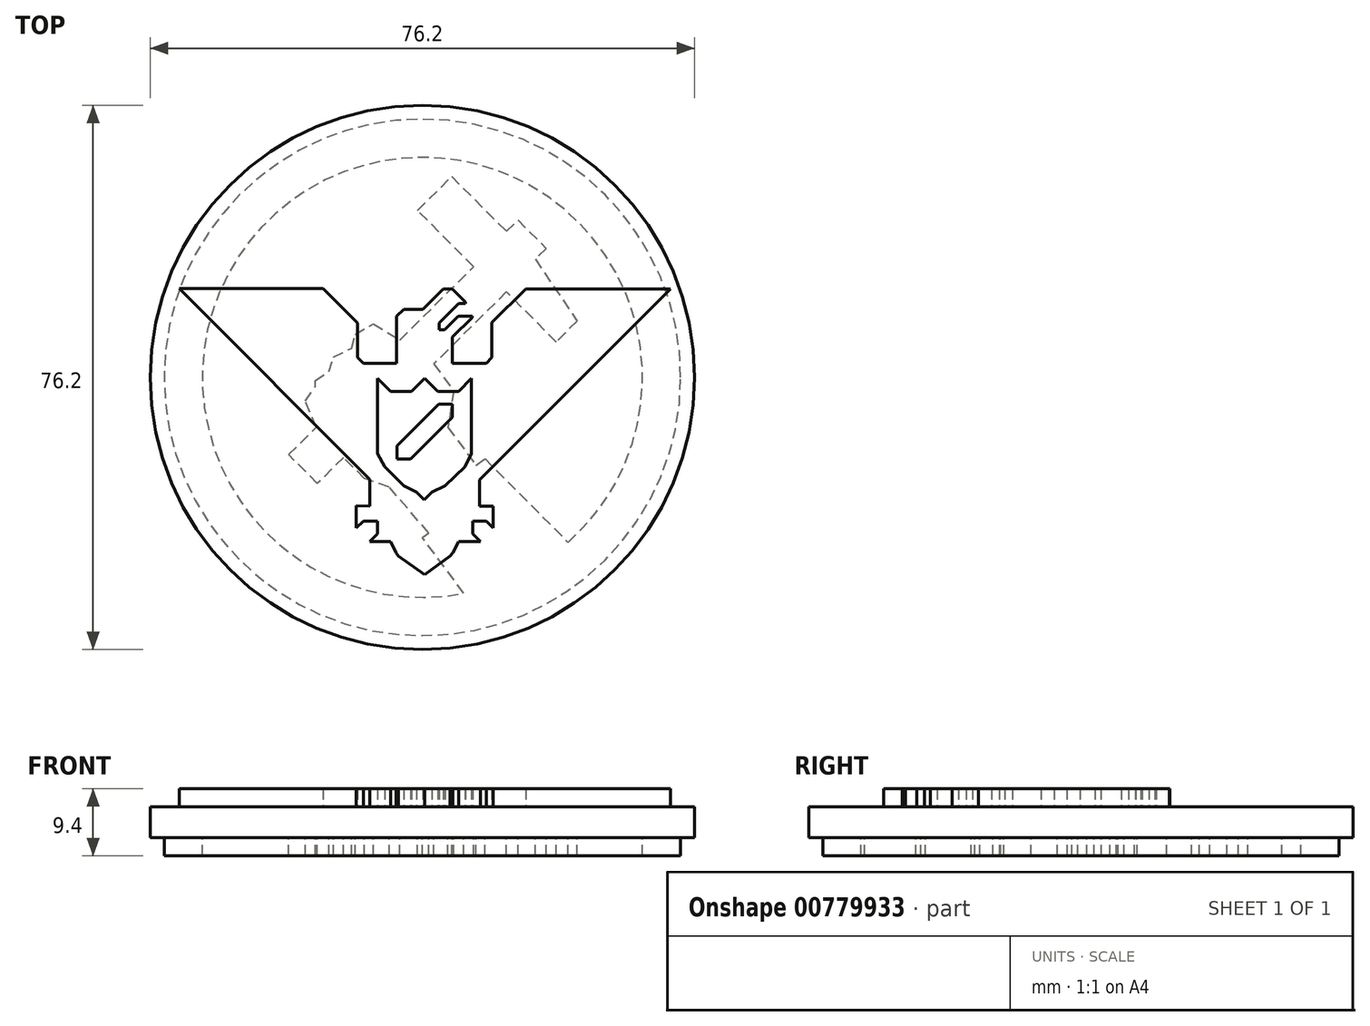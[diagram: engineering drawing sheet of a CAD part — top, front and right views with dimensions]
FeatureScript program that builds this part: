
annotation { "Feature Type Name" : "Feature", "Feature Type Description" : "" }
export const myFeature = defineFeature(function(context is Context, id is Id, definition is map)
    precondition{}
    {
        {
            var Q0;
            Q0=qCreatedBy(makeId("Top.planeOp"),FACE);
            var sketch = newSketch(context, id + "F0", { "sketchPlane" : qUnion([Q0])});
            skCircle(sketch, "E0", {"center": v(0, 0) * mm, "radius": 38.1 * mm});
            skSolve(sketch);
        }
        {
            var Q0;
            Q0=makeQuery(id+"F0.imprint","IMPRINT",FACE,{"disambiguationData":[TD([[makeQuery(id+"F0.imprint","IMPRINT",EDGE,{"derivedFrom":sQuery(id+"F0.wireOp",EDGE,"E0")}),1.0]])]});
            extrude(context, id + "F1", {"entities" : qUnion([Q0]), "depth" : 4.32 * mm, "offsetDistance" : 25.4 * mm});
        }
        {
            var Q0;
            Q0=makeQuery(id+"F1.opExtrude","CAP_FACE",FACE,{"disambiguationData":[OSD([sQuery(id+"F0.wireOp",EDGE,"E0")])],"isStart":false});
            var sketch = newSketch(context, id + "F2", { "sketchPlane" : qUnion([Q0])});
            skLineSegment(sketch, "E1", {"start": v(-7.37, -14.31) * mm, "end": v(-34.06, 12.44) * mm});
            skLineSegment(sketch, "E2", {"start": v(-34.06, 12.44) * mm, "end": v(-13.93, 12.44) * mm});
            skLineSegment(sketch, "E3", {"start": v(-13.93, 12.44) * mm, "end": v(-9.08, 7.65) * mm});
            skLineSegment(sketch, "E4", {"start": v(-9.08, 7.65) * mm, "end": v(-9.08, 2.8) * mm});
            skLineSegment(sketch, "E5", {"start": v(-9.08, 2.8) * mm, "end": v(-8.26, 1.95) * mm});
            skLineSegment(sketch, "E6", {"start": v(-8.26, 1.95) * mm, "end": v(-3.6, 1.95) * mm});
            skLineSegment(sketch, "E7", {"start": v(-3.6, 1.95) * mm, "end": v(-3.6, 8.56) * mm});
            skLineSegment(sketch, "E8", {"start": v(-3.6, 8.56) * mm, "end": v(-2.59, 9.55) * mm});
            skLineSegment(sketch, "E9", {"start": v(-2.59, 9.55) * mm, "end": v(0.09, 9.55) * mm});
            skLineSegment(sketch, "E10", {"start": v(0.09, 9.55) * mm, "end": v(2.92, 12.4) * mm});
            skLineSegment(sketch, "E11", {"start": v(2.92, 12.4) * mm, "end": v(4.16, 12.4) * mm});
            skLineSegment(sketch, "E12", {"start": v(4.16, 12.4) * mm, "end": v(6, 10.56) * mm});
            skLineSegment(sketch, "E13", {"start": v(6, 10.56) * mm, "end": v(6, 10.37) * mm});
            skLineSegment(sketch, "E14", {"start": v(6, 10.37) * mm, "end": v(5.08, 10.37) * mm});
            skLineSegment(sketch, "E15", {"start": v(5.08, 10.37) * mm, "end": v(2.35, 7.62) * mm});
            skLineSegment(sketch, "E16", {"start": v(2.35, 7.62) * mm, "end": v(2.35, 6.67) * mm});
            skLineSegment(sketch, "E17", {"start": v(2.35, 6.67) * mm, "end": v(3.1, 6.67) * mm});
            skLineSegment(sketch, "E18", {"start": v(3.1, 6.67) * mm, "end": v(4.99, 8.56) * mm});
            skLineSegment(sketch, "E19", {"start": v(4.99, 8.56) * mm, "end": v(6.96, 8.56) * mm});
            skLineSegment(sketch, "E20", {"start": v(6.96, 8.56) * mm, "end": v(6.96, 8.36) * mm});
            skLineSegment(sketch, "E21", {"start": v(6.96, 8.36) * mm, "end": v(4.19, 5.62) * mm});
            skLineSegment(sketch, "E22", {"start": v(4.19, 5.62) * mm, "end": v(4.19, 1.99) * mm});
            skLineSegment(sketch, "E23", {"start": v(4.19, 1.99) * mm, "end": v(8.94, 1.99) * mm});
            skLineSegment(sketch, "E24", {"start": v(8.94, 1.99) * mm, "end": v(9.73, 2.79) * mm});
            skLineSegment(sketch, "E25", {"start": v(9.73, 2.79) * mm, "end": v(9.73, 7.67) * mm});
            skLineSegment(sketch, "E26", {"start": v(9.73, 7.67) * mm, "end": v(14.5, 12.4) * mm});
            skLineSegment(sketch, "E27", {"start": v(14.5, 12.4) * mm, "end": v(34.76, 12.4) * mm});
            skLineSegment(sketch, "E28", {"start": v(8.02, -14.32) * mm, "end": v(8.02, -18) * mm});
            skLineSegment(sketch, "E29", {"start": v(8.02, -18) * mm, "end": v(9.9, -18) * mm});
            skLineSegment(sketch, "E30", {"start": v(9.9, -18) * mm, "end": v(9.9, -21.1) * mm});
            skLineSegment(sketch, "E31", {"start": v(9.9, -21.1) * mm, "end": v(8.96, -20.1) * mm});
            skLineSegment(sketch, "E32", {"start": v(8.96, -20.1) * mm, "end": v(7.05, -20.1) * mm});
            skLineSegment(sketch, "E33", {"start": v(7.05, -20.1) * mm, "end": v(7.05, -21.9) * mm});
            skLineSegment(sketch, "E34", {"start": v(7.05, -21.9) * mm, "end": v(8.1, -22.96) * mm});
            skLineSegment(sketch, "E35", {"start": v(8.1, -22.96) * mm, "end": v(5.08, -22.96) * mm});
            skLineSegment(sketch, "E36", {"start": v(5.08, -22.96) * mm, "end": v(4.29, -24.6) * mm});
            skLineSegment(sketch, "E37", {"start": v(4.29, -24.6) * mm, "end": v(3.85, -25.02) * mm});
            skLineSegment(sketch, "E38", {"start": v(3.85, -25.02) * mm, "end": v(0.32, -27.6) * mm});
            skLineSegment(sketch, "E39", {"start": v(0.32, -27.6) * mm, "end": v(-3.34, -25.02) * mm});
            skLineSegment(sketch, "E40", {"start": v(-3.34, -25.02) * mm, "end": v(-3.65, -24.6) * mm});
            skLineSegment(sketch, "E41", {"start": v(-3.65, -24.6) * mm, "end": v(-4.43, -22.96) * mm});
            skLineSegment(sketch, "E42", {"start": v(-4.43, -22.96) * mm, "end": v(-7.37, -22.96) * mm});
            skLineSegment(sketch, "E43", {"start": v(-7.37, -22.96) * mm, "end": v(-6.3, -21.9) * mm});
            skLineSegment(sketch, "E44", {"start": v(-6.3, -21.9) * mm, "end": v(-6.3, -20.1) * mm});
            skLineSegment(sketch, "E45", {"start": v(-6.3, -20.1) * mm, "end": v(-8.25, -20.1) * mm});
            skLineSegment(sketch, "E46", {"start": v(-8.25, -20.1) * mm, "end": v(-9.25, -21.08) * mm});
            skLineSegment(sketch, "E47", {"start": v(-9.25, -21.08) * mm, "end": v(-9.25, -18) * mm});
            skLineSegment(sketch, "E48", {"start": v(-7.37, -14.31) * mm, "end": v(-7.37, -18) * mm});
            skLineSegment(sketch, "E49", {"start": v(-7.37, -18) * mm, "end": v(-9.25, -18) * mm});
            skLineSegment(sketch, "E50", {"start": v(-6.3, -0.11) * mm, "end": v(-6.3, -10.67) * mm});
            skLineSegment(sketch, "E51", {"start": v(-6.3, -10.67) * mm, "end": v(-5.26, -12.48) * mm});
            skLineSegment(sketch, "E52", {"start": v(-5.26, -12.48) * mm, "end": v(-2.59, -15.2) * mm});
            skLineSegment(sketch, "E53", {"start": v(-2.59, -15.2) * mm, "end": v(-0.8, -16.08) * mm});
            skLineSegment(sketch, "E54", {"start": v(-0.8, -16.08) * mm, "end": v(0.25, -17.16) * mm});
            skLineSegment(sketch, "E55", {"start": v(0.25, -17.16) * mm, "end": v(1.35, -16.08) * mm});
            skLineSegment(sketch, "E56", {"start": v(1.35, -16.08) * mm, "end": v(3.2, -15.2) * mm});
            skLineSegment(sketch, "E57", {"start": v(3.2, -15.2) * mm, "end": v(5.97, -12.48) * mm});
            skLineSegment(sketch, "E58", {"start": v(5.97, -12.48) * mm, "end": v(6.86, -10.67) * mm});
            skLineSegment(sketch, "E59", {"start": v(6.86, -10.67) * mm, "end": v(6.86, -0.11) * mm});
            skLineSegment(sketch, "E60", {"start": v(6.86, -0.11) * mm, "end": v(5.06, -1.94) * mm});
            skLineSegment(sketch, "E61", {"start": v(5.06, -1.94) * mm, "end": v(2.18, -1.94) * mm});
            skLineSegment(sketch, "E62", {"start": v(34.76, 12.4) * mm, "end": v(8.02, -14.32) * mm});
            skLineSegment(sketch, "E63", {"start": v(-6.3, -0.11) * mm, "end": v(-4.46, -1.94) * mm});
            skLineSegment(sketch, "E64", {"start": v(-4.46, -1.94) * mm, "end": v(-1.51, -1.94) * mm});
            skLineSegment(sketch, "E65", {"start": v(-1.51, -1.94) * mm, "end": v(0.32, -0.11) * mm});
            skLineSegment(sketch, "E66", {"start": v(0.32, -0.11) * mm, "end": v(2.18, -1.94) * mm});
            skLineSegment(sketch, "E67", {"start": v(4.17, -5.6) * mm, "end": v(-1.67, -11.44) * mm});
            skLineSegment(sketch, "E68", {"start": v(-1.67, -11.44) * mm, "end": v(-3.57, -11.44) * mm});
            skLineSegment(sketch, "E69", {"start": v(-3.57, -11.44) * mm, "end": v(-3.57, -9.6) * mm});
            skLineSegment(sketch, "E70", {"start": v(-3.57, -9.6) * mm, "end": v(2.28, -3.72) * mm});
            skLineSegment(sketch, "E71", {"start": v(2.28, -3.72) * mm, "end": v(4.17, -3.72) * mm});
            skLineSegment(sketch, "E72", {"start": v(4.17, -3.72) * mm, "end": v(4.17, -5.6) * mm});
            skSolve(sketch);
        }
        {
            var Q0;
            Q0=makeQuery(id+"F2.imprint","IMPRINT",FACE,{"disambiguationData":[TD([[makeQuery(id+"F2.imprint","IMPRINT",EDGE,{"derivedFrom":sQuery(id+"F2.wireOp",EDGE,"E1")}),-1.0]])]});
            var Q1;
            Q1=makeQuery(id+"F2.imprint","IMPRINT",FACE,{"disambiguationData":[TD([[makeQuery(id+"F2.imprint","IMPRINT",EDGE,{"derivedFrom":sQuery(id+"F2.wireOp",EDGE,"E67")}),-1.0]])]});
            extrude(context, id + "F3", {"entities" : qUnion([Q0, Q1]), "operationType" : NewBodyOperationType.ADD, "depth" : 2.54 * mm, "offsetDistance" : 25.4 * mm});
        }
        {
            var Q0;
            Q0=qCreatedBy(makeId("Top.planeOp"),FACE);
            var sketch = newSketch(context, id + "F4", { "sketchPlane" : qUnion([Q0])});
            skCircle(sketch, "E73", {"center": v(0, 0) * mm, "radius": 30.8 * mm});
            skLineSegment(sketch, "E74", {"start": v(5.8, -30.26) * mm, "end": v(0, -22.44) * mm});
            skLineSegment(sketch, "E75", {"start": v(0, -22.44) * mm, "end": v(0.9, -21.78) * mm});
            skLineSegment(sketch, "E76", {"start": v(0.9, -21.78) * mm, "end": v(-4.66, -15.36) * mm});
            skLineSegment(sketch, "E77", {"start": v(-4.66, -15.36) * mm, "end": v(-8.1, -14.18) * mm});
            skLineSegment(sketch, "E78", {"start": v(-8.1, -14.18) * mm, "end": v(-11.05, -11.22) * mm});
            skLineSegment(sketch, "E79", {"start": v(-11.05, -11.22) * mm, "end": v(-14.71, -14.85) * mm});
            skLineSegment(sketch, "E80", {"start": v(-14.71, -14.85) * mm, "end": v(-18.72, -10.82) * mm});
            skLineSegment(sketch, "E81", {"start": v(-18.72, -10.82) * mm, "end": v(-14.88, -7) * mm});
            skLineSegment(sketch, "E82", {"start": v(-14.88, -7) * mm, "end": v(-16.39, -3.31) * mm});
            skLineSegment(sketch, "E83", {"start": v(-16.39, -3.31) * mm, "end": v(-15, -1.25) * mm});
            skLineSegment(sketch, "E84", {"start": v(-15, -1.25) * mm, "end": v(-15, -0.47) * mm});
            skLineSegment(sketch, "E85", {"start": v(-15, -0.47) * mm, "end": v(-13.06, 0.8) * mm});
            skLineSegment(sketch, "E86", {"start": v(-13.06, 0.8) * mm, "end": v(-12.48, 2.84) * mm});
            skLineSegment(sketch, "E87", {"start": v(-12.48, 2.84) * mm, "end": v(-9.93, 4.09) * mm});
            skLineSegment(sketch, "E88", {"start": v(-9.93, 4.09) * mm, "end": v(-9.4, 6.03) * mm});
            skLineSegment(sketch, "E89", {"start": v(-9.4, 6.03) * mm, "end": v(-6.89, 7.48) * mm});
            skLineSegment(sketch, "E90", {"start": v(-6.89, 7.48) * mm, "end": v(-3.15, 5.23) * mm});
            skLineSegment(sketch, "E91", {"start": v(-3.15, 5.23) * mm, "end": v(7.16, 15.48) * mm});
            skLineSegment(sketch, "E92", {"start": v(7.16, 15.48) * mm, "end": v(-0.68, 23.37) * mm});
            skLineSegment(sketch, "E93", {"start": v(-0.68, 23.37) * mm, "end": v(4.11, 28.13) * mm});
            skLineSegment(sketch, "E94", {"start": v(4.11, 28.13) * mm, "end": v(11.76, 20.43) * mm});
            skLineSegment(sketch, "E95", {"start": v(11.76, 20.43) * mm, "end": v(13.37, 22.03) * mm});
            skLineSegment(sketch, "E96", {"start": v(13.37, 22.03) * mm, "end": v(17.3, 18.06) * mm});
            skLineSegment(sketch, "E97", {"start": v(17.3, 18.06) * mm, "end": v(15.78, 16.54) * mm});
            skLineSegment(sketch, "E98", {"start": v(15.78, 16.54) * mm, "end": v(21.67, 7.9) * mm});
            skLineSegment(sketch, "E99", {"start": v(21.67, 7.9) * mm, "end": v(18.73, 4.97) * mm});
            skLineSegment(sketch, "E100", {"start": v(18.73, 4.97) * mm, "end": v(11.76, 11.98) * mm});
            skLineSegment(sketch, "E101", {"start": v(11.76, 11.98) * mm, "end": v(1.6, 1.87) * mm});
            skLineSegment(sketch, "E102", {"start": v(1.6, 1.87) * mm, "end": v(4.37, -1.9) * mm});
            skLineSegment(sketch, "E103", {"start": v(4.37, -1.9) * mm, "end": v(3.57, -7) * mm});
            skLineSegment(sketch, "E104", {"start": v(3.57, -7) * mm, "end": v(7.5, -12.3) * mm});
            skLineSegment(sketch, "E105", {"start": v(7.5, -12.3) * mm, "end": v(8.75, -11.39) * mm});
            skLineSegment(sketch, "E106", {"start": v(8.75, -11.39) * mm, "end": v(13.93, -16.6) * mm});
            skLineSegment(sketch, "E107", {"start": v(13.93, -16.6) * mm, "end": v(20.39, -23.1) * mm});
            skCircle(sketch, "E108", {"center": v(0, 0) * mm, "radius": 36.16 * mm});
            skSolve(sketch);
        }
        {
            var Q0;
            Q0=makeQuery(id+"F4.imprint","IMPRINT",FACE,{"disambiguationData":[TD([[makeQuery(id+"F4.imprint","IMPRINT",EDGE,{"derivedFrom":sQuery(id+"F4.wireOp",EDGE,"E108")}),1.0]])]});
            var Q1;
            {var subQ0=sQuery(id+"F4.wireOp",EDGE,"E74");Q1=makeQuery(id+"F4.imprint","IMPRINT",FACE,{"disambiguationData":[TD([[makeQuery(id+"F4.imprint","IMPRINT",EDGE,{"derivedFrom":subQ0}),-1.0]])]});}
            extrude(context, id + "F5", {"entities" : qUnion([Q0, Q1]), "operationType" : NewBodyOperationType.ADD, "oppositeDirection" : true, "depth" : 2.54 * mm, "offsetDistance" : 25.4 * mm});
        }
    });
